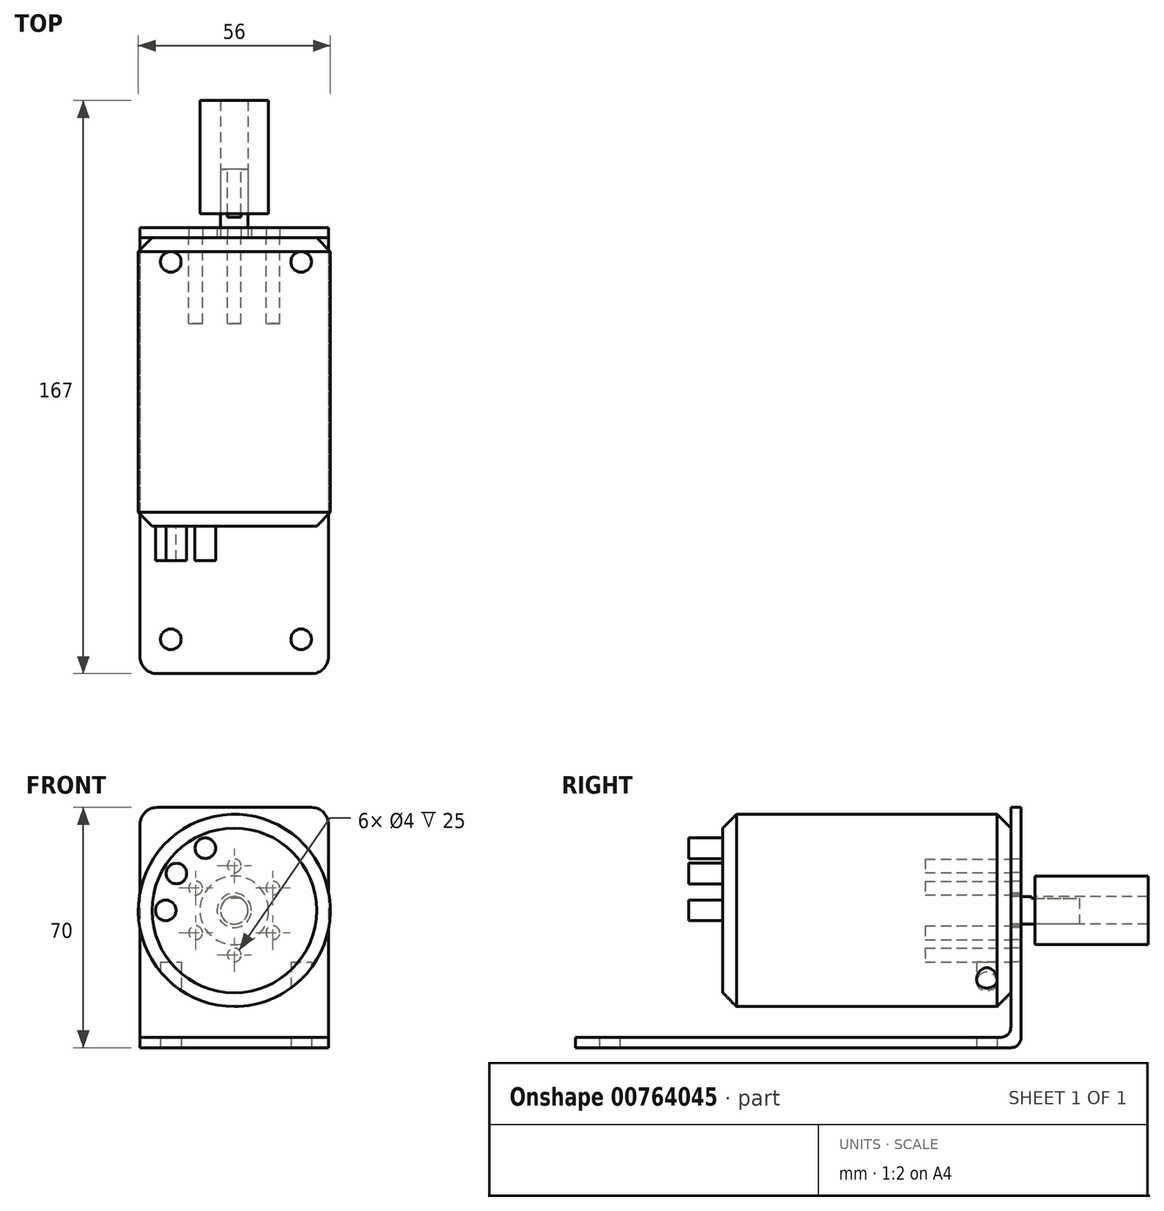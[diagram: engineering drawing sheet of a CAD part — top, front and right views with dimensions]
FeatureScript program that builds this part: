
annotation { "Feature Type Name" : "Feature", "Feature Type Description" : "" }
export const myFeature = defineFeature(function(context is Context, id is Id, definition is map)
    precondition{}
    {
        {
            var Q0;
            Q0=qCreatedBy(makeId("Front.planeOp"),FACE);
            var sketch = newSketch(context, id + "F0", { "sketchPlane" : qUnion([Q0])});
            skCircle(sketch, "E0", {"center": v(0, 0) * mm, "radius": 28 * mm});
            skSolve(sketch);
        }
        {
            var Q0;
            Q0=makeQuery(id+"F0.imprint","IMPRINT",FACE,{"disambiguationData":[TD([[makeQuery(id+"F0.imprint","IMPRINT",EDGE,{"derivedFrom":sQuery(id+"F0.wireOp",EDGE,"E0")}),1.0]])]});
            extrude(context, id + "F1", {"entities" : qUnion([Q0]), "depth" : 84 * mm, "offsetDistance" : 25 * mm});
        }
        {
            var Q0;
            Q0=makeQuery(id+"F1.opExtrude","CAP_FACE",FACE,{"disambiguationData":[OSD([sQuery(id+"F0.wireOp",EDGE,"E0")])],"isStart":true});
            var sketch = newSketch(context, id + "F2", { "sketchPlane" : qUnion([Q0])});
            skCircle(sketch, "E1", {"center": v(0, 0) * mm, "radius": 4 * mm});
            skSolve(sketch);
        }
        {
            var Q0;
            Q0=makeQuery(id+"F2.imprint","IMPRINT",FACE,{"disambiguationData":[TD([[makeQuery(id+"F2.imprint","IMPRINT",EDGE,{"derivedFrom":sQuery(id+"F2.wireOp",EDGE,"E1")}),1.0]])]});
            extrude(context, id + "F3", {"entities" : qUnion([Q0]), "operationType" : NewBodyOperationType.ADD, "depth" : 20 * mm, "offsetDistance" : 25 * mm});
        }
        {
            var Q0;
            Q0=makeQuery(id+"F1.opExtrude","CAP_EDGE",EDGE,{"disambiguationData":[OSD([sQuery(id+"F0.wireOp",EDGE,"E0")])],"isStart":true});
            var Q1;
            Q1=makeQuery(id+"F1.opExtrude","CAP_EDGE",EDGE,{"disambiguationData":[OSD([sQuery(id+"F0.wireOp",EDGE,"E0")])],"isStart":false});
            chamfer(context, id + "F4", {"entities" : qUnion([Q0, Q1]), "width" : 4 * mm, "tangentPropagation" : true});
        }
        {
            var Q0;
            Q0=makeQuery(id+"F1.opExtrude","CAP_FACE",FACE,{"disambiguationData":[OSD([sQuery(id+"F0.wireOp",EDGE,"E0")])],"isStart":true});
            var sketch = newSketch(context, id + "F5", { "sketchPlane" : qUnion([Q0])});
            skCircle(sketch, "E2", {"center": v(0, 13) * mm, "radius": 2 * mm});
            skCircle(sketch, "E3.1.0", {"center": v(-11.26, 6.5) * mm, "radius": 2 * mm});
            skCircle(sketch, "E3.2.0", {"center": v(-11.26, -6.5) * mm, "radius": 2 * mm});
            skCircle(sketch, "E3.3.0", {"center": v(0, -13) * mm, "radius": 2 * mm});
            skCircle(sketch, "E3.4.0", {"center": v(11.26, -6.5) * mm, "radius": 2 * mm});
            skCircle(sketch, "E3.5.0", {"center": v(11.26, 6.5) * mm, "radius": 2 * mm});
            skPoint(sketch, "E3.center", {"position": v(0, 0) * mm});
            skSolve(sketch);
        }
        {
            var Q0;
            Q0 = qSketchRegion(id + "F5", true);
            extrude(context, id + "F6", {"entities" : qUnion([Q0]), "operationType" : NewBodyOperationType.REMOVE, "oppositeDirection" : true, "depth" : 25 * mm, "offsetDistance" : 25 * mm});
        }
        {
            var Q0;
            Q0=makeQuery(id+"F3.opExtrude","CAP_FACE",FACE,{"disambiguationData":[OSD([sQuery(id+"F2.wireOp",EDGE,"E1")])],"isStart":false});
            var sketch = newSketch(context, id + "F7", { "sketchPlane" : qUnion([Q0])});
            skArc(sketch, "E4.0", {"start": v(1.98, 3.47) * mm, "mid": v(0, 4) * mm, "end": v(-1.98, 3.47) * mm});
            skLineSegment(sketch, "E5", {"start": v(-1.98, 3.47) * mm, "end": v(1.98, 3.47) * mm});
            skSolve(sketch);
        }
        {
            var Q0;
            Q0 = qSketchRegion(id + "F7", true);
            extrude(context, id + "F8", {"entities" : qUnion([Q0]), "operationType" : NewBodyOperationType.REMOVE, "oppositeDirection" : true, "depth" : 14 * mm, "offsetDistance" : 25 * mm});
        }
        {
            var Q0;
            Q0=makeQuery(id+"F1.opExtrude","CAP_FACE",FACE,{"disambiguationData":[OSD([sQuery(id+"F0.wireOp",EDGE,"E0")])],"isStart":false});
            var sketch = newSketch(context, id + "F9", { "sketchPlane" : qUnion([Q0])});
            skCircle(sketch, "E6", {"center": v(-20, 0) * mm, "radius": 3 * mm});
            skCircle(sketch, "E7.1.0", {"center": v(-16.87, 10.75) * mm, "radius": 3 * mm});
            skCircle(sketch, "E7.2.0", {"center": v(-8.45, 18.13) * mm, "radius": 3 * mm});
            skPoint(sketch, "E7.center", {"position": v(0, 0) * mm});
            skLineSegment(sketch, "E7.anchor1", {"start": v(0, 0) * mm, "end": v(-20, 0) * mm, "construction": true});
            skLineSegment(sketch, "E7.anchor2", {"start": v(0, 0) * mm, "end": v(-8.45, 18.13) * mm, "construction": true});
            skSolve(sketch);
        }
        {
            var Q0;
            Q0 = qSketchRegion(id + "F9", true);
            extrude(context, id + "F10", {"entities" : qUnion([Q0]), "operationType" : NewBodyOperationType.ADD, "depth" : 10 * mm, "offsetDistance" : 25 * mm});
        }
        {
            var Q0;
            Q0=makeQuery(id+"F1.opExtrude","CAP_FACE",FACE,{"disambiguationData":[OSD([sQuery(id+"F0.wireOp",EDGE,"E0")])],"isStart":true});
            var sketch = newSketch(context, id + "F11", { "sketchPlane" : qUnion([Q0])});
            skLineSegment(sketch, "E8.bottom", {"start": v(-27.5, 30) * mm, "end": v(27.5, 30) * mm});
            skLineSegment(sketch, "E8.top", {"start": v(-27.5, -40) * mm, "end": v(27.5, -40) * mm});
            skLineSegment(sketch, "E8.left", {"start": v(-27.5, 30) * mm, "end": v(-27.5, -40) * mm});
            skLineSegment(sketch, "E8.right", {"start": v(27.5, 30) * mm, "end": v(27.5, -40) * mm});
            skCircle(sketch, "E9", {"center": v(0, 0) * mm, "radius": 5 * mm});
            skCircle(sketch, "E10.0", {"center": v(0, 13) * mm, "radius": 2 * mm});
            skCircle(sketch, "E11.0", {"center": v(11.26, 6.5) * mm, "radius": 2 * mm});
            skCircle(sketch, "E12.0.0", {"center": v(0, 0) * mm, "radius": 24 * mm});
            skCircle(sketch, "E13.0", {"center": v(0, -13) * mm, "radius": 2 * mm});
            skCircle(sketch, "E14.0", {"center": v(-11.26, -6.5) * mm, "radius": 2 * mm});
            skCircle(sketch, "E15.0", {"center": v(-11.26, 6.5) * mm, "radius": 2 * mm});
            skCircle(sketch, "E16.0", {"center": v(11.26, -6.5) * mm, "radius": 2 * mm});
            skSolve(sketch);
        }
        {
            var Q0;
            Q0 = qSketchRegion(id + "F11", true);
            var Q1;
            Q1=makeQuery(id+"F11.imprint","IMPRINT",FACE,{"disambiguationData":[TD([[makeQuery(id+"F11.imprint","IMPRINT",EDGE,{"derivedFrom":sQuery(id+"F11.wireOp",EDGE,"E9")}),-1.0]])]});
            extrude(context, id + "F12", {"entities" : qUnion([Q0, Q1]), "depth" : 3 * mm, "offsetDistance" : 25 * mm});
        }
        {
            var Q0;
            Q0=makeQuery(id+"F12.opExtrude","SWEPT_FACE",FACE,{"disambiguationData":[OSD([sQuery(id+"F11.wireOp",EDGE,"E8.right")])]});
            var sketch = newSketch(context, id + "F13", { "sketchPlane" : qUnion([Q0])});
            skLineSegment(sketch, "E17.bottom", {"start": v(-3, -40) * mm, "end": v(127, -40) * mm});
            skLineSegment(sketch, "E17.top", {"start": v(-3, -37) * mm, "end": v(127, -37) * mm});
            skLineSegment(sketch, "E17.left", {"start": v(-3, -40) * mm, "end": v(-3, -37) * mm});
            skLineSegment(sketch, "E17.right", {"start": v(127, -40) * mm, "end": v(127, -37) * mm});
            skSolve(sketch);
        }
        {
            var Q0;
            Q0 = qSketchRegion(id + "F13", true);
            extrude(context, id + "F14", {"entities" : qUnion([Q0]), "operationType" : NewBodyOperationType.ADD, "oppositeDirection" : true, "depth" : 55 * mm, "offsetDistance" : 25 * mm});
        }
        {
            var Q0;
            Q0=makeQuery(id+"F12.opExtrude","SWEPT_EDGE",EDGE,{"disambiguationData":[OSD([sQuery(id+"F11.wireOp",EDGE,"E8.bottom"),sQuery(id+"F11.wireOp",EDGE,"E8.left")])]});
            var Q1;
            Q1=makeQuery(id+"F12.opExtrude","SWEPT_EDGE",EDGE,{"disambiguationData":[OSD([sQuery(id+"F11.wireOp",EDGE,"E8.bottom"),sQuery(id+"F11.wireOp",EDGE,"E8.right")])]});
            var Q2;
            Q2=makeQuery(id+"F14.opExtrude","CAP_EDGE",EDGE,{"disambiguationData":[OSD([sQuery(id+"F13.wireOp",EDGE,"E17.right")])],"isStart":false});
            var Q3;
            Q3=makeQuery(id+"F14.opExtrude","CAP_EDGE",EDGE,{"disambiguationData":[OSD([sQuery(id+"F13.wireOp",EDGE,"E17.right")])],"isStart":true});
            fillet(context, id + "F15", {"entities" : qUnion([Q0, Q1, Q2, Q3]), "radius" : 5 * mm, "tangentPropagation" : true, "allowEdgeOverflow" : false});
        }
        {
            var Q0;
            Q0=makeQuery(id+"F14.boolean.opBoolean","MERGE",FACE,{"derivedFrom":[makeQuery(id+"F12.opExtrude","SWEPT_FACE",FACE,{"disambiguationData":[OSD([sQuery(id+"F11.wireOp",EDGE,"E8.top")])]}),makeQuery(id+"F14.opExtrude","SWEPT_FACE",FACE,{"disambiguationData":[OSD([sQuery(id+"F13.wireOp",EDGE,"E17.bottom")])]})]});
            var sketch = newSketch(context, id + "F16", { "sketchPlane" : qUnion([Q0])});
            skCircle(sketch, "E18", {"center": v(19.5, 117) * mm, "radius": 3 * mm});
            skCircle(sketch, "E19.0.1.0", {"center": v(19.5, 7) * mm, "radius": 3 * mm});
            skCircle(sketch, "E19.1.0.0", {"center": v(-18.5, 117) * mm, "radius": 3 * mm});
            skCircle(sketch, "E19.1.1.0", {"center": v(-18.5, 7) * mm, "radius": 3 * mm});
            skLineSegment(sketch, "E19.direction1", {"start": v(19.5, 117) * mm, "end": v(-18.5, 117) * mm, "construction": true});
            skLineSegment(sketch, "E19.direction2", {"start": v(19.5, 117) * mm, "end": v(19.5, 7) * mm, "construction": true});
            skSolve(sketch);
        }
        {
            var Q0;
            Q0 = qSketchRegion(id + "F16", true);
            extrude(context, id + "F17", {"entities" : qUnion([Q0]), "operationType" : NewBodyOperationType.REMOVE, "oppositeDirection" : true, "depth" : 25 * mm, "offsetDistance" : 25 * mm});
        }
        {
            var Q0;
            Q0=makeQuery(id+"F14.boolean.opBoolean","INTERSECT",EDGE,{"derivedFrom":[makeQuery(id+"F12.opExtrude","CAP_FACE",FACE,{"disambiguationData":[OSD([sQuery(id+"F11.wireOp",EDGE,"E8.bottom"),sQuery(id+"F11.wireOp",EDGE,"E8.top"),sQuery(id+"F11.wireOp",EDGE,"E8.left"),sQuery(id+"F11.wireOp",EDGE,"E8.right"),sQuery(id+"F11.wireOp",EDGE,"E9"),sQuery(id+"F11.wireOp",EDGE,"E10.0"),sQuery(id+"F11.wireOp",EDGE,"E11.0"),sQuery(id+"F11.wireOp",EDGE,"E13.0"),sQuery(id+"F11.wireOp",EDGE,"E14.0"),sQuery(id+"F11.wireOp",EDGE,"E15.0"),sQuery(id+"F11.wireOp",EDGE,"E16.0")])],"isStart":true}),makeQuery(id+"F14.opExtrude","SWEPT_FACE",FACE,{"disambiguationData":[OSD([sQuery(id+"F13.wireOp",EDGE,"E17.top")])]})]});
            var Q1;
            Q1=makeQuery(id+"F12.opExtrude","CAP_EDGE",EDGE,{"disambiguationData":[OSD([sQuery(id+"F11.wireOp",EDGE,"E8.top")])],"isStart":false});
            fillet(context, id + "F18", {"entities" : qUnion([Q0, Q1]), "radius" : 3 * mm, "tangentPropagation" : true, "allowEdgeOverflow" : false});
        }
        {
            var Q0;
            Q0=makeQuery(id+"F3.opExtrude","CAP_FACE",FACE,{"disambiguationData":[OSD([sQuery(id+"F2.wireOp",EDGE,"E1")])],"isStart":false});
            var sketch = newSketch(context, id + "F19", { "sketchPlane" : qUnion([Q0])});
            skCircle(sketch, "E20", {"center": v(0, 0) * mm, "radius": 10 * mm});
            skArc(sketch, "E21.0", {"start": v(-1.98, 3.47) * mm, "mid": v(0, -4) * mm, "end": v(1.98, 3.47) * mm});
            skArc(sketch, "E22.0", {"start": v(1.98, 3.47) * mm, "mid": v(0, 4) * mm, "end": v(-1.98, 3.47) * mm});
            skSolve(sketch);
        }
        {
            var Q0;
            Q0=makeQuery(id+"F19.imprint","IMPRINT",FACE,{"disambiguationData":[TD([[makeQuery(id+"F19.imprint","IMPRINT",EDGE,{"derivedFrom":sQuery(id+"F19.wireOp",EDGE,"E20")}),1.0]])]});
            extrude(context, id + "F20", {"entities" : qUnion([Q0]), "depth" : 20 * mm, "offsetDistance" : 25 * mm, "hasSecondDirection" : true, "secondDirectionOppositeDirection" : true, "secondDirectionDepth" : 13 * mm});
        }
    });
